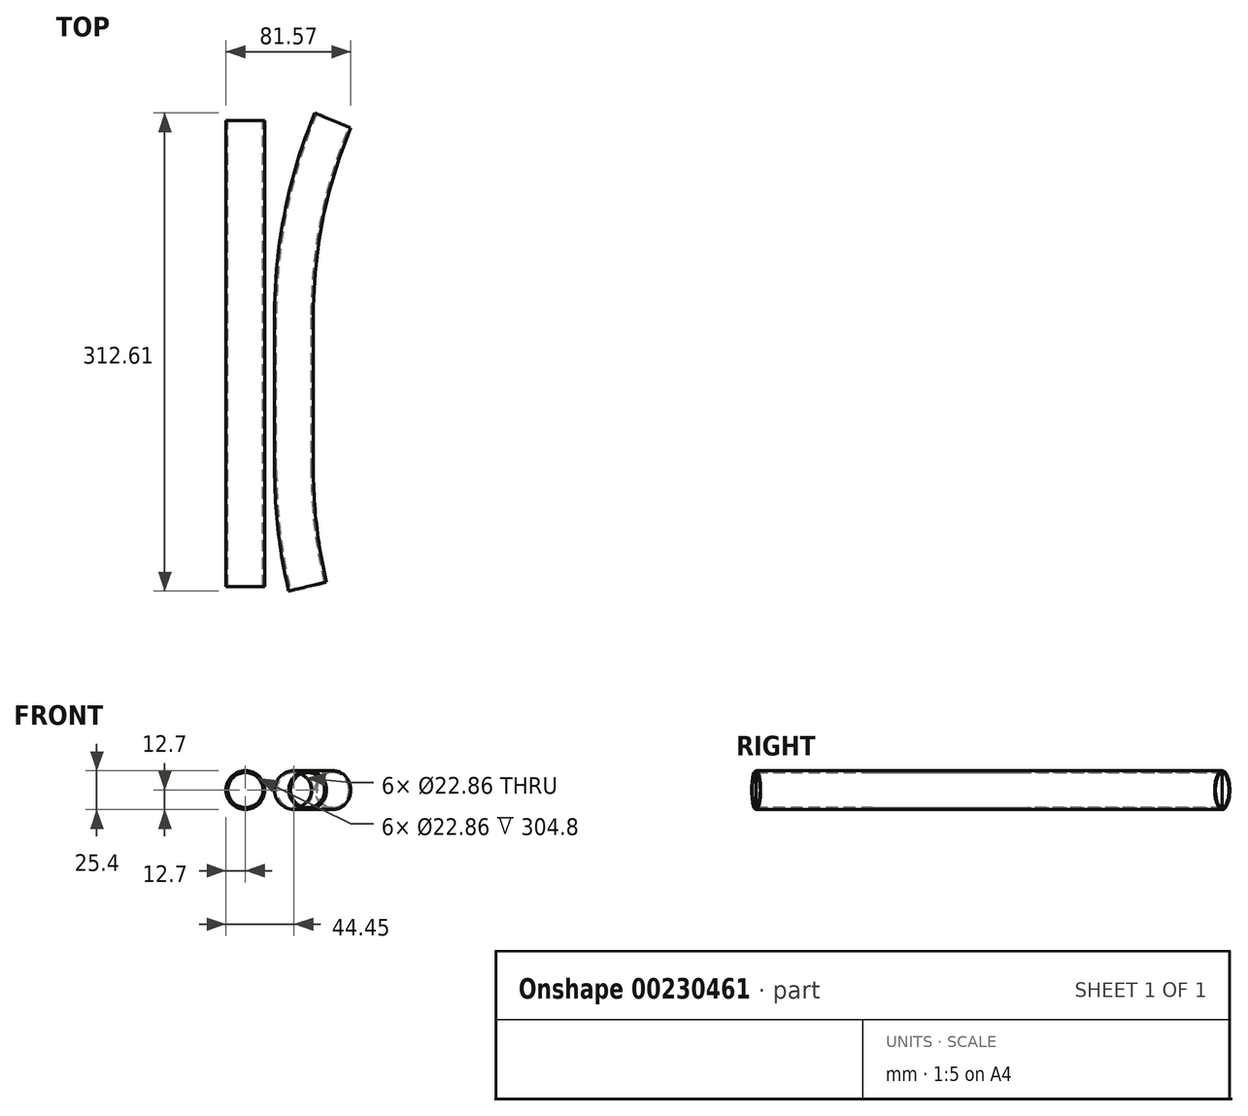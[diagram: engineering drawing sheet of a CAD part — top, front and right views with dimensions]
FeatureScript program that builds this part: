
annotation { "Feature Type Name" : "Feature", "Feature Type Description" : "" }
export const myFeature = defineFeature(function(context is Context, id is Id, definition is map)
    precondition{}
    {
        {
            var Q0;
            Q0=qCreatedBy(makeId("Top.planeOp"),FACE);
            var sketch = newSketch(context, id + "F0", { "sketchPlane" : qUnion([Q0])});
            skLineSegment(sketch, "E0", {"start": v(0, 0) * mm, "end": v(0, 304.8) * mm});
            skLineSegment(sketch, "E1", {"start": v(31.75, 76.2) * mm, "end": v(31.75, 177.8) * mm});
            skArc(sketch, "E2", {"start": v(31.75, 177.8) * mm, "mid": v(38.16, 242.56) * mm, "end": v(57.15, 304.8) * mm});
            skArc(sketch, "E3", {"start": v(31.75, 76.2) * mm, "mid": v(33.99, 37.84) * mm, "end": v(40.66, 0) * mm});
            skSolve(sketch);
        }
        {
            var Q0;
            Q0=qCreatedBy(makeId("Front.planeOp"),FACE);
            var sketch = newSketch(context, id + "F1", { "sketchPlane" : qUnion([Q0])});
            skCircle(sketch, "E4", {"center": v(0, 0) * mm, "radius": 12.7 * mm});
            skCircle(sketch, "E5.0", {"center": v(0, 0) * mm, "radius": 11.43 * mm});
            skSolve(sketch);
        }
        {
            var Q0;
            Q0 = qSketchRegion(id + "F1", true);
            var Q1;
            Q1=sQuery(id+"F0.wireOp",EDGE,"E0");
            sweep(context, id + "F2", {"profiles" : qUnion([Q0]), "path" : qUnion([Q1])});
        }
        {
            var Q0;
            Q0=sQuery(id+"F0.wireOp",EDGE,"E3");
            var Q1;
            Q1=sQuery(id+"F0.wireOp",VERTEX,"E3.end");
            cPlane(context, id + "F3", {"entities" : qUnion([Q0, Q1]), "cplaneType" : CPlaneType.CURVE_POINT, "offset" : 25.4 * mm, "width" : 152.4 * mm, "height" : 152.4 * mm});
        }
        {
            var Q0;
            Q0=qCreatedBy(id+"F3.planeOp",FACE);
            var sketch = newSketch(context, id + "F4", { "sketchPlane" : qUnion([Q0])});
            skCircle(sketch, "E6", {"center": v(39.57, 0) * mm, "radius": 12.7 * mm});
            skCircle(sketch, "E7.0", {"center": v(39.57, 0) * mm, "radius": 11.43 * mm});
            skSolve(sketch);
        }
        {
            var Q0;
            Q0 = qSketchRegion(id + "F4", true);
            var Q1;
            Q1=sQuery(id+"F0.wireOp",EDGE,"E3");
            var Q2;
            Q2=sQuery(id+"F0.wireOp",EDGE,"E1");
            var Q3;
            Q3=sQuery(id+"F0.wireOp",EDGE,"E2");
            sweep(context, id + "F5", {"profiles" : qUnion([Q0]), "path" : qUnion([Q1, Q2, Q3])});
        }
        {
            var Q0;
            Q0=qCreatedBy(makeId("Front.planeOp"),FACE);
            cPlane(context, id + "F6", {"entities" : qUnion([Q0]), "cplaneType" : CPlaneType.OFFSET, "offset" : 127 * mm, "oppositeDirection" : true, "width" : 152.4 * mm, "height" : 152.4 * mm});
        }
        {
            var Q0;
            Q0=qCreatedBy(id+"F6.planeOp",FACE);
            var sketch = newSketch(context, id + "F7", { "sketchPlane" : qUnion([Q0])});
            skLineSegment(sketch, "E8", {"start": v(0, 0) * mm, "end": v(-8.98, -8.98) * mm});
            skLineSegment(sketch, "E9", {"start": v(31.75, 0) * mm, "end": v(40.73, -8.98) * mm});
            skLineSegment(sketch, "E10", {"start": v(-31.11, 44.45) * mm, "end": v(62.86, 44.45) * mm});
            skArc(sketch, "E11", {"start": v(40.73, -8.98) * mm, "mid": v(91.78, 1.17) * mm, "end": v(62.86, 44.45) * mm});
            skArc(sketch, "E12", {"start": v(-8.98, -8.98) * mm, "mid": v(-60.03, 1.17) * mm, "end": v(-31.11, 44.45) * mm});
            skSolve(sketch);
        }
        {
            var Q0;
            Q0=sQuery(id+"F7.wireOp",EDGE,"E8");
            var Q1;
            Q1=sQuery(id+"F7.wireOp",VERTEX,"E8.start");
            cPlane(context, id + "F8", {"entities" : qUnion([Q0, Q1]), "cplaneType" : CPlaneType.CURVE_POINT, "offset" : 25.4 * mm, "width" : 152.4 * mm, "height" : 152.4 * mm});
        }
        {
            var Q0;
            Q0=qCreatedBy(id+"F8.planeOp",FACE);
            var sketch = newSketch(context, id + "F9", { "sketchPlane" : qUnion([Q0])});
            skCircle(sketch, "E13", {"center": v(-127, 0) * mm, "radius": 9.53 * mm});
            skCircle(sketch, "E14.0", {"center": v(-127, 0) * mm, "radius": 8.26 * mm});
            skSolve(sketch);
        }
        {
            var Q0;
            Q0 = qSketchRegion(id + "F9", true);
            var Q1;
            Q1 = qConstructionFilter(qBodyType(qCreatedBy(id + "F7" ,EDGE), BodyType.WIRE), ConstructionObject.NO);
            sweep(context, id + "F10", {"profiles" : qUnion([Q0]), "path" : qUnion([Q1])});
        }
        {
            var Q0;
            Q0=makeQuery(id+"F2.opSweep","SWEPT_BODY",BODY,{"disambiguationData":[OSD([sQuery(id+"F0.wireOp",EDGE,"E0"),sQuery(id+"F1.wireOp",EDGE,"E4"),sQuery(id+"F1.wireOp",EDGE,"E5.0")])]});
            var Q1;
            Q1=makeQuery(id+"F5.opSweep","SWEPT_BODY",BODY,{"disambiguationData":[OSD([sQuery(id+"F0.wireOp",EDGE,"E2"),sQuery(id+"F4.wireOp",EDGE,"E6"),sQuery(id+"F4.wireOp",EDGE,"E7.0")])]});
            var Q2;
            Q2=makeQuery(id+"F10.opSweep","SWEPT_BODY",BODY,{"disambiguationData":[OSD([sQuery(id+"F7.wireOp",EDGE,"E9"),sQuery(id+"F9.wireOp",EDGE,"E13"),sQuery(id+"F9.wireOp",EDGE,"E14.0")])]});
            booleanBodies(context, id + "F11", {"operationType" : BooleanOperationType.SUBTRACTION, "tools" : qUnion([Q0, Q1]), "targets" : qUnion([Q2]), "keepTools" : true});
        }
        {
            var Q0;
            Q0=makeQuery(id+"F11.opBoolean","SPLIT",BODY,{"disambiguationData":[OD(1.0)],"derivedFrom":makeQuery(id+"F10.opSweep","SWEPT_BODY",BODY,{"disambiguationData":[OSD([sQuery(id+"F7.wireOp",EDGE,"E9"),sQuery(id+"F9.wireOp",EDGE,"E13"),sQuery(id+"F9.wireOp",EDGE,"E14.0")])]})});
            var Q1;
            Q1=makeQuery(id+"F11.opBoolean","SPLIT",BODY,{"disambiguationData":[OD(0.0)],"derivedFrom":makeQuery(id+"F10.opSweep","SWEPT_BODY",BODY,{"disambiguationData":[OSD([sQuery(id+"F7.wireOp",EDGE,"E9"),sQuery(id+"F9.wireOp",EDGE,"E13"),sQuery(id+"F9.wireOp",EDGE,"E14.0")])]})});
            deleteBodies(context, id + "F12", {"entities" : qUnion([Q0, Q1])});
        }
    });
